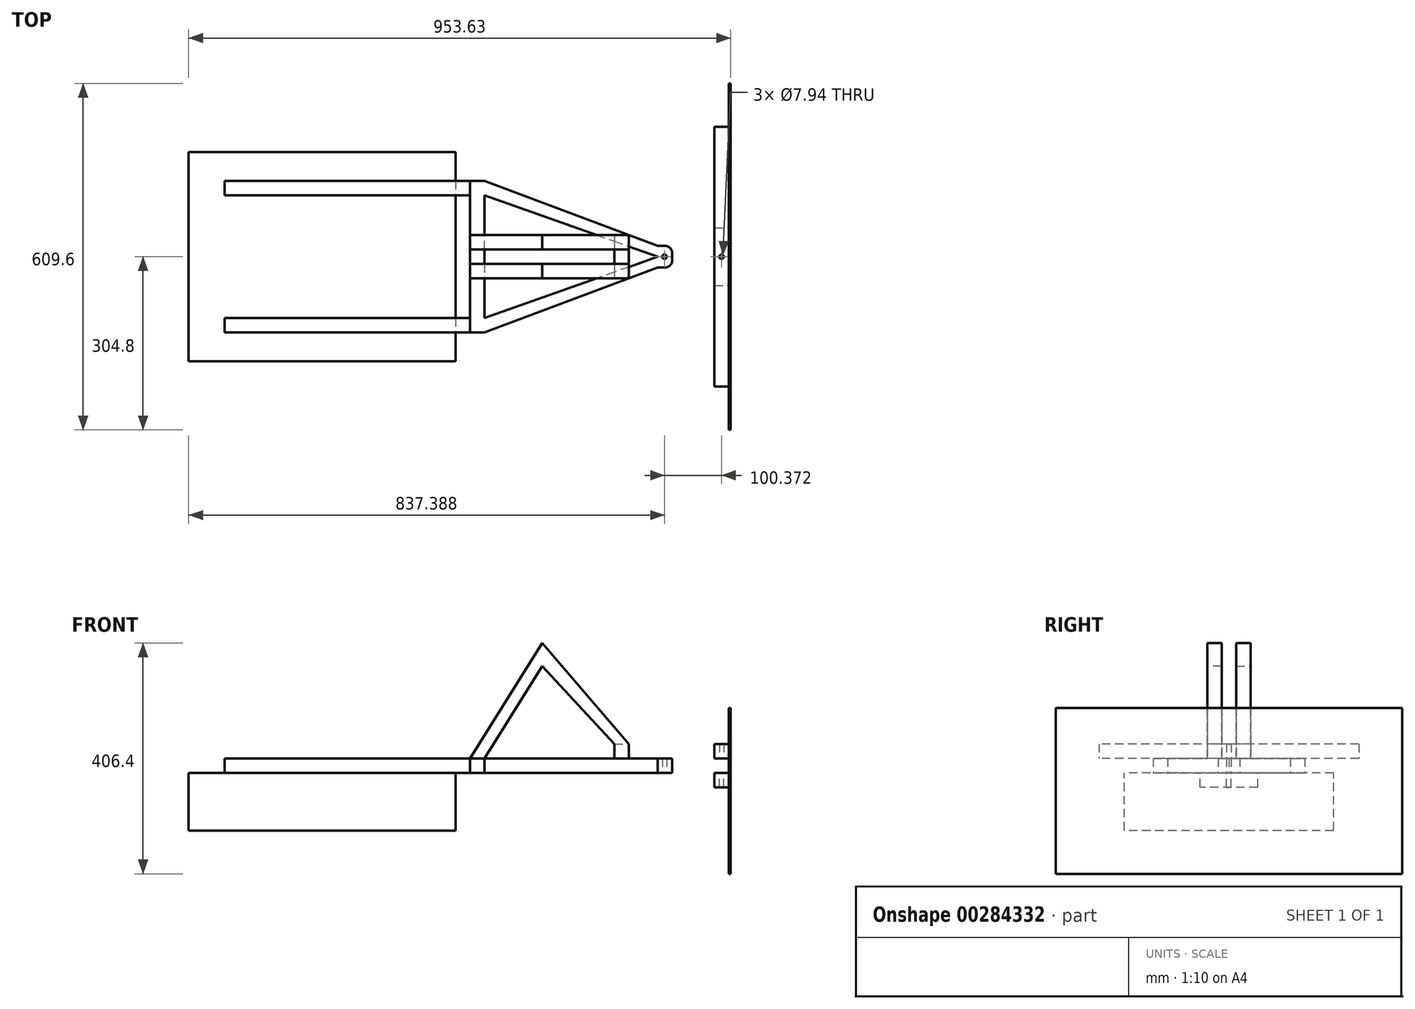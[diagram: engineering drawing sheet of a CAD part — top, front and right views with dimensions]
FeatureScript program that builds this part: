
annotation { "Feature Type Name" : "Feature", "Feature Type Description" : "" }
export const myFeature = defineFeature(function(context is Context, id is Id, definition is map)
    precondition{}
    {
        {
            var Q0;
            Q0=qCreatedBy(makeId("Top.planeOp"),FACE);
            var sketch = newSketch(context, id + "F0", { "sketchPlane" : qUnion([Q0])});
            skLineSegment(sketch, "E0.bottom", {"start": v(234.95, 184.15) * mm, "end": v(-234.95, 184.15) * mm});
            skLineSegment(sketch, "E0.top", {"start": v(234.95, -184.15) * mm, "end": v(-234.95, -184.15) * mm});
            skLineSegment(sketch, "E0.left", {"start": v(234.95, 184.15) * mm, "end": v(234.95, -184.15) * mm});
            skLineSegment(sketch, "E0.right", {"start": v(-234.95, 184.15) * mm, "end": v(-234.95, -184.15) * mm});
            skPoint(sketch, "E0.middle", {"position": v(0, 0) * mm});
            skSolve(sketch);
        }
        {
            var Q0;
            Q0=makeQuery(id+"F0.imprint","IMPRINT",FACE,{"disambiguationData":[TD([[makeQuery(id+"F0.imprint","IMPRINT",EDGE,{"derivedFrom":sQuery(id+"F0.wireOp",EDGE,"E0.bottom")}),1.0]])]});
            var sketch = newSketch(context, id + "F1", { "sketchPlane" : qUnion([Q0])});
            skLineSegment(sketch, "E1", {"start": v(-314.18, 0) * mm, "end": v(719, 0) * mm, "construction": true});
            skLineSegment(sketch, "E2.bottom", {"start": v(-171.45, 133.35) * mm, "end": v(260.35, 133.35) * mm});
            skLineSegment(sketch, "E2.top", {"start": v(-171.45, 107.95) * mm, "end": v(260.35, 107.95) * mm});
            skLineSegment(sketch, "E2.left", {"start": v(-171.45, 133.35) * mm, "end": v(-171.45, 107.95) * mm});
            skLineSegment(sketch, "E2.right", {"start": v(260.35, 133.35) * mm, "end": v(260.35, 107.95) * mm});
            skLineSegment(sketch, "E3.MirrorCS", {"start": v(-171.45, -133.35) * mm, "end": v(260.35, -133.35) * mm});
            skLineSegment(sketch, "E4.MirrorCS", {"start": v(-171.45, -133.35) * mm, "end": v(-171.45, -107.95) * mm});
            skLineSegment(sketch, "E5.MirrorCS", {"start": v(-171.45, -107.95) * mm, "end": v(260.35, -107.95) * mm});
            skLineSegment(sketch, "E6.MirrorCS", {"start": v(260.35, -133.35) * mm, "end": v(260.35, -107.95) * mm});
            skSolve(sketch);
        }
        {
            var Q0;
            {var subQ0=sQuery(id+"F1.wireOp",EDGE,"E4.MirrorCS");Q0=makeQuery(id+"F1.imprint","IMPRINT",FACE,{"disambiguationData":[TD([[makeQuery(id+"F1.imprint","IMPRINT",EDGE,{"derivedFrom":subQ0}),-1.0]])]});}
            var Q1;
            {var subQ0=sQuery(id+"F1.wireOp",EDGE,"E2.left");Q1=makeQuery(id+"F1.imprint","IMPRINT",FACE,{"disambiguationData":[TD([[makeQuery(id+"F1.imprint","IMPRINT",EDGE,{"derivedFrom":subQ0}),1.0]])]});}
            var Q2;
            {var subQ0=sQuery(id+"F1.wireOp",EDGE,"E6.MirrorCS");Q2=makeQuery(id+"F1.imprint","IMPRINT",FACE,{"disambiguationData":[TD([[makeQuery(id+"F1.imprint","IMPRINT",EDGE,{"derivedFrom":subQ0}),1.0]])]});}
            var Q3;
            {var subQ0=sQuery(id+"F1.wireOp",EDGE,"E2.right");Q3=makeQuery(id+"F1.imprint","IMPRINT",FACE,{"disambiguationData":[TD([[makeQuery(id+"F1.imprint","IMPRINT",EDGE,{"derivedFrom":subQ0}),-1.0]])]});}
            extrude(context, id + "F2", {"entities" : qUnion([Q0, Q1, Q2, Q3]), "depth" : 25.4 * mm});
        }
        {
            var Q0;
            Q0=makeQuery(id+"F2.opExtrude","SWEPT_FACE",FACE,{"disambiguationData":[OSD([sQuery(id+"F1.wireOp",EDGE,"E6.MirrorCS")])]});
            var sketch = newSketch(context, id + "F3", { "sketchPlane" : qUnion([Q0])});
            skLineSegment(sketch, "E7.0", {"start": v(133.35, 25.4) * mm, "end": v(133.35, 0) * mm});
            skLineSegment(sketch, "E8.bottom", {"start": v(-133.35, 25.4) * mm, "end": v(133.35, 25.4) * mm});
            skLineSegment(sketch, "E8.top", {"start": v(-133.35, 0) * mm, "end": v(133.35, 0) * mm});
            skLineSegment(sketch, "E8.left", {"start": v(-133.35, 25.4) * mm, "end": v(-133.35, 0) * mm});
            skSolve(sketch);
        }
        {
            var Q0;
            {var subQ2=sQuery(id+"F3.wireOp",EDGE,"E7.0");Q0=makeQuery(id+"F3.imprint","IMPRINT",FACE,{"disambiguationData":[TD([[makeQuery(id+"F3.imprint","IMPRINT",EDGE,{"derivedFrom":subQ2}),-1.0]])]});}
            var Q1;
            {var subQ0=sQuery(id+"F3.wireOp",EDGE,"E8.left");Q1=makeQuery(id+"F3.imprint","IMPRINT",FACE,{"disambiguationData":[TD([[makeQuery(id+"F3.imprint","IMPRINT",EDGE,{"derivedFrom":subQ0}),1.0]])]});}
            extrude(context, id + "F4", {"entities" : qUnion([Q0, Q1]), "depth" : 25.4 * mm});
        }
        {
            var Q0;
            Q0=makeQuery(id+"F0.imprint","IMPRINT",FACE,{"disambiguationData":[TD([[makeQuery(id+"F0.imprint","IMPRINT",EDGE,{"derivedFrom":sQuery(id+"F0.wireOp",EDGE,"E0.bottom")}),1.0]])]});
            extrude(context, id + "F5", {"entities" : qUnion([Q0]), "oppositeDirection" : true, "depth" : 101.6 * mm});
        }
        {
            var Q0;
            Q0=makeQuery(id+"F5.opExtrude","CAP_FACE",FACE,{"disambiguationData":[OSD([sQuery(id+"F0.wireOp",EDGE,"E0.bottom"),sQuery(id+"F0.wireOp",EDGE,"E0.top"),sQuery(id+"F0.wireOp",EDGE,"E0.left"),sQuery(id+"F0.wireOp",EDGE,"E0.right")])],"isStart":true});
            var sketch = newSketch(context, id + "F6", { "sketchPlane" : qUnion([Q0])});
            skLineSegment(sketch, "E9", {"start": v(0, 0) * mm, "end": v(748.8, 0) * mm, "construction": true});
            skLineSegment(sketch, "E10.0.0", {"start": v(260.35, 133.35) * mm, "end": v(260.35, -133.35) * mm});
            skLineSegment(sketch, "E10.0.1", {"start": v(260.35, -133.35) * mm, "end": v(285.75, -133.35) * mm});
            skLineSegment(sketch, "E10.0.2", {"start": v(285.75, -133.35) * mm, "end": v(285.75, 133.35) * mm});
            skLineSegment(sketch, "E10.0.3", {"start": v(285.75, 133.35) * mm, "end": v(260.35, 133.35) * mm});
            skLineSegment(sketch, "E11", {"start": v(285.75, 107.95) * mm, "end": v(590.55, 0) * mm});
            skLineSegment(sketch, "E12", {"start": v(590.55, 0) * mm, "end": v(285.75, -107.95) * mm});
            skLineSegment(sketch, "E13", {"start": v(285.75, -107.95) * mm, "end": v(285.75, -133.35) * mm});
            skLineSegment(sketch, "E14", {"start": v(590.55, 19.05) * mm, "end": v(590.55, -19.05) * mm});
            skLineSegment(sketch, "E15", {"start": v(590.55, 19.05) * mm, "end": v(285.75, 133.35) * mm});
            skLineSegment(sketch, "E16", {"start": v(590.55, -19.05) * mm, "end": v(285.75, -133.35) * mm});
            skLineSegment(sketch, "E17", {"start": v(590.55, 19.05) * mm, "end": v(615.95, 19.05) * mm});
            skLineSegment(sketch, "E18", {"start": v(615.95, 19.05) * mm, "end": v(615.95, -19.05) * mm});
            skLineSegment(sketch, "E19", {"start": v(615.95, -19.05) * mm, "end": v(590.55, -19.05) * mm});
            skCircle(sketch, "E20", {"center": v(602.44, 0) * mm, "radius": 3.97 * mm});
            skSolve(sketch);
        }
        {
            var Q0;
            {var subQ0=sQuery(id+"F6.wireOp",EDGE,"E12");Q0=makeQuery(id+"F6.imprint","IMPRINT",FACE,{"disambiguationData":[TD([[makeQuery(id+"F6.imprint","IMPRINT",EDGE,{"derivedFrom":subQ0}),1.0]])]});}
            var Q1;
            {var subQ2=sQuery(id+"F6.wireOp",EDGE,"E11");Q1=makeQuery(id+"F6.imprint","IMPRINT",FACE,{"disambiguationData":[TD([[makeQuery(id+"F6.imprint","IMPRINT",EDGE,{"derivedFrom":subQ2}),1.0]])]});}
            var Q2;
            {var subQ0=sQuery(id+"F6.wireOp",EDGE,"E17");Q2=makeQuery(id+"F6.imprint","IMPRINT",FACE,{"disambiguationData":[TD([[makeQuery(id+"F6.imprint","IMPRINT",EDGE,{"derivedFrom":subQ0}),-1.0]])]});}
            extrude(context, id + "F7", {"entities" : qUnion([Q0, Q1, Q2]), "operationType" : NewBodyOperationType.ADD, "depth" : 25.4 * mm});
        }
        {
            var Q0;
            Q0=makeQuery(id+"F7.boolean.opBoolean","MERGE",FACE,{"derivedFrom":[makeQuery(id+"F4.opExtrude","SWEPT_FACE",FACE,{"disambiguationData":[OSD([sQuery(id+"F3.wireOp",EDGE,"E8.bottom")])]}),makeQuery(id+"F7.opExtrude","CAP_FACE",FACE,{"disambiguationData":[OSD([sQuery(id+"F6.wireOp",EDGE,"E10.0.2"),sQuery(id+"F6.wireOp",EDGE,"E11"),sQuery(id+"F6.wireOp",EDGE,"E12"),sQuery(id+"F6.wireOp",EDGE,"E13"),sQuery(id+"F6.wireOp",EDGE,"E15"),sQuery(id+"F6.wireOp",EDGE,"E16"),sQuery(id+"F6.wireOp",EDGE,"E17"),sQuery(id+"F6.wireOp",EDGE,"E18"),sQuery(id+"F6.wireOp",EDGE,"E19"),sQuery(id+"F6.wireOp",EDGE,"E20")])],"isStart":false})]});
            var sketch = newSketch(context, id + "F8", { "sketchPlane" : qUnion([Q0])});
            skLineSegment(sketch, "E21", {"start": v(0, 0) * mm, "end": v(894.48, 0) * mm, "construction": true});
            skPoint(sketch, "E21.endSnap0", {"position": v(234.95, 0) * mm});
            skLineSegment(sketch, "E22.bottom", {"start": v(690.1, 228.6) * mm, "end": v(715.5, 228.6) * mm});
            skLineSegment(sketch, "E22.top", {"start": v(690.1, -228.6) * mm, "end": v(715.5, -228.6) * mm});
            skLineSegment(sketch, "E22.left", {"start": v(690.1, 228.6) * mm, "end": v(690.1, -228.6) * mm});
            skLineSegment(sketch, "E22.right", {"start": v(715.5, 228.6) * mm, "end": v(715.5, -228.6) * mm});
            skPoint(sketch, "E22.middle", {"position": v(702.8, 0) * mm});
            skCircle(sketch, "E23", {"center": v(702.8, 0) * mm, "radius": 3.97 * mm});
            skSolve(sketch);
        }
        {
            var Q0;
            Q0=makeQuery(id+"F8.imprint","IMPRINT",FACE,{"disambiguationData":[TD([[makeQuery(id+"F8.imprint","IMPRINT",EDGE,{"derivedFrom":sQuery(id+"F8.wireOp",EDGE,"E22.bottom")}),-1.0]])]});
            extrude(context, id + "F9", {"entities" : qUnion([Q0]), "depth" : 25.4 * mm});
        }
        {
            var Q0;
            Q0=makeQuery(id+"F7.boolean.opBoolean","MERGE",FACE,{"derivedFrom":[makeQuery(id+"F4.opExtrude","SWEPT_FACE",FACE,{"disambiguationData":[OSD([sQuery(id+"F3.wireOp",EDGE,"E8.top")])]}),makeQuery(id+"F7.opExtrude","CAP_FACE",FACE,{"disambiguationData":[OSD([sQuery(id+"F6.wireOp",EDGE,"E10.0.2"),sQuery(id+"F6.wireOp",EDGE,"E11"),sQuery(id+"F6.wireOp",EDGE,"E12"),sQuery(id+"F6.wireOp",EDGE,"E13"),sQuery(id+"F6.wireOp",EDGE,"E15"),sQuery(id+"F6.wireOp",EDGE,"E16"),sQuery(id+"F6.wireOp",EDGE,"E17"),sQuery(id+"F6.wireOp",EDGE,"E18"),sQuery(id+"F6.wireOp",EDGE,"E19"),sQuery(id+"F6.wireOp",EDGE,"E20")])],"isStart":true})]});
            var sketch = newSketch(context, id + "F10", { "sketchPlane" : qUnion([Q0])});
            skLineSegment(sketch, "E24.0.0", {"start": v(690.1, 228.6) * mm, "end": v(690.1, -228.6) * mm});
            skLineSegment(sketch, "E24.0.1", {"start": v(690.1, -228.6) * mm, "end": v(715.5, -228.6) * mm});
            skLineSegment(sketch, "E24.0.2", {"start": v(715.5, -228.6) * mm, "end": v(715.5, 228.6) * mm});
            skLineSegment(sketch, "E24.0.3", {"start": v(715.5, 228.6) * mm, "end": v(690.1, 228.6) * mm});
            skLineSegment(sketch, "E25", {"start": v(0, 0) * mm, "end": v(841.55, 0) * mm, "construction": true});
            skLineSegment(sketch, "E26.bottom", {"start": v(690.1, 50.8) * mm, "end": v(715.5, 50.8) * mm});
            skLineSegment(sketch, "E26.top", {"start": v(690.1, -50.8) * mm, "end": v(715.5, -50.8) * mm});
            skLineSegment(sketch, "E26.left", {"start": v(690.1, 50.8) * mm, "end": v(690.1, -50.8) * mm});
            skLineSegment(sketch, "E26.right", {"start": v(715.5, 50.8) * mm, "end": v(715.5, -50.8) * mm});
            skCircle(sketch, "E27.0", {"center": v(702.8, 0) * mm, "radius": 3.97 * mm});
            skSolve(sketch);
        }
        {
            var Q0;
            Q0=makeQuery(id+"F10.imprint","IMPRINT",FACE,{"disambiguationData":[TD([[makeQuery(id+"F10.imprint","IMPRINT",EDGE,{"derivedFrom":sQuery(id+"F10.wireOp",EDGE,"E26.bottom")}),-1.0]])]});
            extrude(context, id + "F11", {"entities" : qUnion([Q0]), "depth" : 25.4 * mm});
        }
        {
            var Q0;
            Q0=makeQuery(id+"F9.opExtrude","SWEPT_FACE",FACE,{"disambiguationData":[OSD([sQuery(id+"F8.wireOp",EDGE,"E22.right")])]});
            var sketch = newSketch(context, id + "F12", { "sketchPlane" : qUnion([Q0])});
            skLineSegment(sketch, "E28", {"start": v(0, -21.2) * mm, "end": v(0, 244.95) * mm, "construction": true});
            skPoint(sketch, "E28.endSnap0", {"position": v(0, 50.8) * mm});
            skLineSegment(sketch, "E29.bottom", {"start": v(-304.8, -177.8) * mm, "end": v(304.8, -177.8) * mm});
            skLineSegment(sketch, "E29.top", {"start": v(-304.8, 114.3) * mm, "end": v(304.8, 114.3) * mm});
            skLineSegment(sketch, "E29.left", {"start": v(-304.8, -177.8) * mm, "end": v(-304.8, 114.3) * mm});
            skLineSegment(sketch, "E29.right", {"start": v(304.8, -177.8) * mm, "end": v(304.8, 114.3) * mm});
            skPoint(sketch, "E29.middle", {"position": v(0, -31.75) * mm});
            skLineSegment(sketch, "E30.MirrorCS", {"start": v(-304.8, 177.8) * mm, "end": v(304.8, 177.8) * mm});
            skSolve(sketch);
        }
        {
            var Q0;
            Q0=makeQuery(id+"F12.imprint","IMPRINT",FACE,{"disambiguationData":[TD([[makeQuery(id+"F12.imprint","IMPRINT",EDGE,{"derivedFrom":sQuery(id+"F12.wireOp",EDGE,"E29.bottom")}),1.0]])]});
            var Q1;
            {var subQ0=sQuery(id+"F8.wireOp",EDGE,"E22.right");Q1=makeQuery(id+"F12.imprint","IMPRINT",FACE,{"disambiguationData":[TD([[makeQuery(id+"F12.imprint","IMPRINT",EDGE,{"derivedFrom":makeQuery(id+"F9.opExtrude","CAP_EDGE",EDGE,{"disambiguationData":[OSD([subQ0])],"isStart":true})}),-1.0]])]});}
            extrude(context, id + "F13", {"entities" : qUnion([Q0, Q1]), "operationType" : NewBodyOperationType.ADD, "depth" : 3.17 * mm});
        }
        {
            var Q0;
            Q0=makeQuery(id+"F7.opExtrude","SWEPT_EDGE",EDGE,{"disambiguationData":[OSD([sQuery(id+"F6.wireOp",EDGE,"E17"),sQuery(id+"F6.wireOp",EDGE,"E18")])]});
            var Q1;
            Q1=makeQuery(id+"F7.opExtrude","SWEPT_EDGE",EDGE,{"disambiguationData":[OSD([sQuery(id+"F6.wireOp",EDGE,"E18"),sQuery(id+"F6.wireOp",EDGE,"E19")])]});
            fillet(context, id + "F14", {"entities" : qUnion([Q0, Q1]), "radius" : 12.7 * mm, "tangentPropagation" : true, "allowEdgeOverflow" : false});
        }
        {
            var Q0;
            Q0=makeQuery(id+"F7.boolean.opBoolean","MERGE",FACE,{"derivedFrom":[makeQuery(id+"F4.opExtrude","SWEPT_FACE",FACE,{"disambiguationData":[OSD([sQuery(id+"F3.wireOp",EDGE,"E8.bottom")])]}),makeQuery(id+"F7.opExtrude","CAP_FACE",FACE,{"disambiguationData":[OSD([sQuery(id+"F6.wireOp",EDGE,"E10.0.2"),sQuery(id+"F6.wireOp",EDGE,"E11"),sQuery(id+"F6.wireOp",EDGE,"E12"),sQuery(id+"F6.wireOp",EDGE,"E13"),sQuery(id+"F6.wireOp",EDGE,"E15"),sQuery(id+"F6.wireOp",EDGE,"E16"),sQuery(id+"F6.wireOp",EDGE,"E17"),sQuery(id+"F6.wireOp",EDGE,"E18"),sQuery(id+"F6.wireOp",EDGE,"E19"),sQuery(id+"F6.wireOp",EDGE,"E20")])],"isStart":false})]});
            var sketch = newSketch(context, id + "F15", { "sketchPlane" : qUnion([Q0])});
            skLineSegment(sketch, "E31", {"start": v(0, 0) * mm, "end": v(756.18, 0) * mm, "construction": true});
            skLineSegment(sketch, "E32.bottom", {"start": v(513.97, 38.1) * mm, "end": v(539.37, 38.1) * mm});
            skLineSegment(sketch, "E32.top", {"start": v(513.97, -38.1) * mm, "end": v(539.37, -38.1) * mm});
            skLineSegment(sketch, "E32.left", {"start": v(513.97, 38.1) * mm, "end": v(513.97, -38.1) * mm});
            skLineSegment(sketch, "E32.right", {"start": v(539.37, 38.1) * mm, "end": v(539.37, -38.1) * mm});
            skPoint(sketch, "E32.middle", {"position": v(526.67, 0) * mm});
            skLineSegment(sketch, "E33.0", {"start": v(285.75, 107.95) * mm, "end": v(590.55, 0) * mm});
            skLineSegment(sketch, "E34.0", {"start": v(590.55, 19.05) * mm, "end": v(285.75, 133.35) * mm});
            skLineSegment(sketch, "E35.0", {"start": v(590.55, 0) * mm, "end": v(285.75, -107.95) * mm});
            skLineSegment(sketch, "E36.0", {"start": v(590.55, -19.05) * mm, "end": v(285.75, -133.35) * mm});
            skSolve(sketch);
        }
        {
            var Q0;
            {var subQ0=sQuery(id+"F15.wireOp",EDGE,"E32.top");Q0=makeQuery(id+"F15.imprint","IMPRINT",FACE,{"disambiguationData":[TD([[makeQuery(id+"F15.imprint","IMPRINT",EDGE,{"derivedFrom":subQ0}),1.0]])]});}
            var Q1;
            {var subQ0=sQuery(id+"F15.wireOp",EDGE,"E33.0");var subQ1=sQuery(id+"F15.wireOp",EDGE,"E32.left");var subQ2=makeQuery(id+"F15.imprint","INTERSECT",VERTEX,{"derivedFrom":[subQ1,subQ0]});Q1=makeQuery(id+"F15.imprint","IMPRINT",FACE,{"disambiguationData":[TD([[makeQuery(id+"F15.imprint","IMPRINT",EDGE,{"disambiguationData":[TD([[subQ2,-1.0]])],"derivedFrom":subQ1}),1.0]])]});}
            var Q2;
            {var subQ0=sQuery(id+"F15.wireOp",EDGE,"E34.0");var subQ1=sQuery(id+"F15.wireOp",EDGE,"E32.left");var subQ2=makeQuery(id+"F15.imprint","INTERSECT",VERTEX,{"derivedFrom":[subQ1,subQ0]});Q2=makeQuery(id+"F15.imprint","IMPRINT",FACE,{"disambiguationData":[TD([[makeQuery(id+"F15.imprint","IMPRINT",EDGE,{"disambiguationData":[TD([[subQ2,-1.0]])],"derivedFrom":subQ1}),1.0]])]});}
            var Q3;
            {var subQ0=sQuery(id+"F15.wireOp",EDGE,"E32.bottom");Q3=makeQuery(id+"F15.imprint","IMPRINT",FACE,{"disambiguationData":[TD([[makeQuery(id+"F15.imprint","IMPRINT",EDGE,{"derivedFrom":subQ0}),-1.0]])]});}
            var Q4;
            {var subQ0=sQuery(id+"F15.wireOp",EDGE,"E36.0");var subQ1=sQuery(id+"F15.wireOp",EDGE,"E32.left");var subQ2=makeQuery(id+"F15.imprint","INTERSECT",VERTEX,{"derivedFrom":[subQ1,subQ0]});Q4=makeQuery(id+"F15.imprint","IMPRINT",FACE,{"disambiguationData":[TD([[makeQuery(id+"F15.imprint","IMPRINT",EDGE,{"disambiguationData":[TD([[subQ2,1.0]])],"derivedFrom":subQ1}),1.0]])]});}
            extrude(context, id + "F16", {"entities" : qUnion([Q0, Q1, Q2, Q3, Q4]), "operationType" : NewBodyOperationType.ADD, "depth" : 25.4 * mm});
        }
        {
            var Q0;
            Q0=makeQuery(id+"F16.opExtrude","SWEPT_FACE",FACE,{"disambiguationData":[OSD([sQuery(id+"F15.wireOp",EDGE,"E32.top")])]});
            var sketch = newSketch(context, id + "F17", { "sketchPlane" : qUnion([Q0])});
            skLineSegment(sketch, "E37.0.1", {"start": v(513.97, 25.4) * mm, "end": v(285.75, 25.4) * mm});
            skLineSegment(sketch, "E37.0.2", {"start": v(285.75, 25.4) * mm, "end": v(260.35, 25.4) * mm});
            skLineSegment(sketch, "E37.0.4", {"start": v(260.35, 25.4) * mm, "end": v(285.75, 25.4) * mm});
            skLineSegment(sketch, "E37.0.5", {"start": v(285.75, 25.4) * mm, "end": v(513.97, 25.4) * mm});
            skLineSegment(sketch, "E37.0.7", {"start": v(513.97, 25.4) * mm, "end": v(285.75, 25.4) * mm});
            skLineSegment(sketch, "E37.0.9", {"start": v(285.75, 25.4) * mm, "end": v(513.97, 25.4) * mm});
            skLineSegment(sketch, "E38", {"start": v(539.37, 50.8) * mm, "end": v(387.35, 228.6) * mm});
            skLineSegment(sketch, "E39", {"start": v(387.35, 228.6) * mm, "end": v(260.35, 25.4) * mm});
            skLineSegment(sketch, "E40", {"start": v(285.75, 25.4) * mm, "end": v(387.35, 187.96) * mm});
            skLineSegment(sketch, "E41", {"start": v(387.35, 187.96) * mm, "end": v(513.97, 50.8) * mm});
            skLineSegment(sketch, "E42", {"start": v(513.97, 50.8) * mm, "end": v(539.37, 50.8) * mm});
            skSolve(sketch);
        }
        {
            var Q0;
            Q0=makeQuery(id+"F17.imprint","IMPRINT",FACE,{"disambiguationData":[TD([[makeQuery(id+"F17.imprint","IMPRINT",EDGE,{"derivedFrom":sQuery(id+"F17.wireOp",EDGE,"E38")}),1.0]])]});
            extrude(context, id + "F18", {"entities" : qUnion([Q0]), "operationType" : NewBodyOperationType.ADD, "oppositeDirection" : true, "depth" : 25.4 * mm});
        }
        {
            var Q0;
            Q0=makeQuery(id+"F16.opExtrude","SWEPT_FACE",FACE,{"disambiguationData":[OSD([sQuery(id+"F15.wireOp",EDGE,"E32.bottom")])]});
            var sketch = newSketch(context, id + "F19", { "sketchPlane" : qUnion([Q0])});
            skLineSegment(sketch, "E43.0", {"start": v(-513.97, 50.8) * mm, "end": v(-539.37, 50.8) * mm});
            skLineSegment(sketch, "E44.0", {"start": v(-539.37, 50.8) * mm, "end": v(-387.35, 228.6) * mm});
            skLineSegment(sketch, "E45.0", {"start": v(-387.35, 187.96) * mm, "end": v(-513.97, 50.8) * mm});
            skLineSegment(sketch, "E46.0", {"start": v(-285.75, 25.4) * mm, "end": v(-387.35, 187.96) * mm});
            skLineSegment(sketch, "E47.0", {"start": v(-387.35, 228.6) * mm, "end": v(-260.35, 25.4) * mm});
            skLineSegment(sketch, "E48.0", {"start": v(-285.75, 25.4) * mm, "end": v(-260.35, 25.4) * mm});
            skSolve(sketch);
        }
        {
            var Q0;
            Q0=makeQuery(id+"F19.imprint","IMPRINT",FACE,{"disambiguationData":[TD([[makeQuery(id+"F19.imprint","IMPRINT",EDGE,{"derivedFrom":sQuery(id+"F19.wireOp",EDGE,"E44.0")}),-1.0]])]});
            extrude(context, id + "F20", {"entities" : qUnion([Q0]), "operationType" : NewBodyOperationType.ADD, "oppositeDirection" : true, "depth" : 25.4 * mm});
        }
    });
